# Revit family: xBall_Valves-Full_Port-WATTS-LFFBV3C_LFFBVS3C_Series
name_source: partatom
category: Pipe Accessories
revit_build: Autodesk Revit 2014 (Build: 20130308_1515(x64)
units: mm (PartAtom-declared; Revit-internal decimal feet)

## types (19) — shared parameters
Connector Description 1 = NPT Connection Inlet
Connector Description 2 = NPT Connection Outlet
Country = United States
Description = 2 Piece, Full Port, Lead Free Brass Ball Valve
Manufacturer = WATTS
Manufacturer Product Line = Water Safety & Flow Control
Material = Lead Free-WATTS-Copper Silicon Alloy
Product Documentation Link = http://media.wattswater.com
Product Page URL = http://www.watts.com
Region = North America
URL = http://www.watts.com

## per-type parameters (varying)
| type | Annotation Circle Radius | Body Midpoint | Center To Body Angle | Center To Handle Angle | Center To Handle Back | Center To Handle Tang | Center To Inlet | Center To Outlet | Connection Radius | Connection Type | Handle Height | Handle Length | Handle Thickness | Handle Width | Inlet Body Radius | Length | Max. Working Pressure | Model | Outlet Body Radius | Stem Height | Stem Radius |
| LFFBV-3C - 0.25" | 0.28 " | 0.875 " | 0.478 " | 0.492 " | 0.275 " | 0.436 " | 0.84 " | 0.91 " | 0" | Female NPT | 0.5 " | 3.438 " | 0.098 " | 0.55 " | 0.35 " | 1.75 " | 600psi (41 bar) WOG, non-shock; 150psi (10.3 bar) WSP | LFFBV-3C | 0.56 " | 1.183 " | 0.31 " |
| LFFBV-3C - 0.375" | 0.28 " | 0.875 " | 0.478 " | 0.492 " | 0.275 " | 0.436 " | 0.84 " | 0.91 " | 0" | Female NPT | 0.5 " | 3.438 " | 0.098 " | 0.55 " | 0.415 " | 1.75 " | 600psi (41 bar) WOG, non-shock; 150psi (10.3 bar) WSP | LFFBV-3C | 0.56 " | 1.183 " | 0.31 " |
| LFFBV-3C - 0.5" | 0.28 " | 0.969 " | 0.46 " | 0.492 " | 0.275 " | 0.436 " | 0.98 " | 0.958 " | 0" | Female NPT | 0.5 " | 3.438 " | 0.098 " | 0.55 " | 0.48 " | 1.938 " | 600psi (41 bar) WOG, non-shock; 150psi (10.3 bar) WSP | LFFBV-3C | 0.56 " | 1.123 " | 0.31 " |
| LFFBV-3C - 0.75" | 0.39 " | 1.157 " | 0.445 " | 0.483 " | 0.345 " | 0.53 " | 1.17 " | 1.143 " | 0" | Female NPT | 0.689 " | 4 " | 0.11 " | 0.689 " | 0.62 " | 2.313 " | 600psi (41 bar) WOG, non-shock; 150psi (10.3 bar) WSP | LFFBV-3C | 0.78 " | 1.359 " | 0.375 " |
| LFFBV-3C - 1" | 0.455 " | 1.407 " | 0.58 " | 0.577 " | 0.404 " | 0.64 " | 1.416 " | 1.397 " | 1" | Female NPT | 0.75 " | 4.25 " | 0.126 " | 0.807 " | 0.75 " | 2.813 " | 600psi (41 bar) WOG, non-shock; 150psi (10.3 bar) WSP | LFFBV-3C | 0.91 " | 1.633 " | 0.465 " |
| LFFBV-3C - 1.25" | 0.575 " | 1.594 " | 0.685 " | 0.577 " | 0.404 " | 0.64 " | 1.587 " | 1.601 " | 1" | Female NPT | 0.75 " | 4.25 " | 0.126 " | 0.807 " | 0.93 " | 3.188 " | 600psi (41 bar) WOG, non-shock; 150psi (10.3 bar) WSP | LFFBV-3C | 1.15 " | 1.823 " | 0.455 " |
| LFFBV-3C - 1.5" | 0.665 " | 1.75 " | 0.815 " | 0.847 " | 0.473 " | 0.687 " | 1.74 " | 1.76 " | 1" | Female NPT | 0.75 " | 5.25 " | 0.157 " | 0.945 " | 1.075 " | 3.5 " | 600psi (41 bar) WOG, non-shock; 150psi (10.3 bar) WSP | LFFBV-3C | 1.33 " | 2.118 " | 0.48 " |
| LFFBV-3C - 2" | 0.845 " | 2.063 " | 0.935 " | 0.847 " | 0.473 " | 0.687 " | 2.029 " | 2.096 " | 1" | Female NPT | 0.75 " | 6 " | 0.157 " | 0.945 " | 1.325 " | 4.125 " | 600psi (41 bar) WOG, non-shock; 150psi (10.3 bar) WSP | LFFBV-3C | 1.69 " | 2.581 " | 0.48 " |
| LFFBV-3C - 2.5" | 1.06 " | 2.657 " | 1.335 " | 0.8 " | 0.473 " | 0.853 " | 2.645 " | 2.668 " | 1" | Female NPT | 0.75 " | 7.375 " | 0.197 " | 0.945 " | 1.597 " | 5.313 " | 400psi (27.5 bar) WOG, non-shock
125psi (8.6 bar) WSP | LFFBV-3C | 2.12 " | 3.055 " | 0.615 " |
| LFFBV-3C - 3" | 1.258 " | 3.032 " | 1.59 " | 0.81 " | 0.551 " | 0.882 " | 3.028 " | 3.035 " | 2" | Female NPT | 0.75 " | 7.75 " | 0.197 " | 1.102 " | 1.98 " | 6.063 " | 400psi (27.5 bar) WOG, non-shock
125psi (8.6 bar) WSP | LFFBV-3C | 2.515 " | 3.477 " | 0.655 " |
| LFFBV-3C - 4" | 1.258 " | 3.719 " | 1.59 " | 0.81 " | 0.551 " | 0.882 " | 3.028 " | 4.41 " | 2" | Female NPT | 0.75 " | 9.625 " | 0.197 " | 1.102 " | 1.98 " | 7.438 " | 400psi (27.5 bar) WOG, non-shock
125psi (8.6 bar) WSP | LFFBV-3C | 2.515 " | 3.477 " | 0.655 " |
| LFFBVS-3C - 0.5" | 0.28 " | 1.032 " | 0.46 " | 0.492 " | 0.275 " | 0.436 " | 0.98 " | 1.083 " | 0" | Soldered Connection | 0.5 " | 3.438 " | 0.098 " | 0.55 " | 0.48 " | 2.063 " | 600psi (41 bar) WOG, non-shock; 150psi (10.3 bar) WSP | LFFBVS-3C | 0.56 " | 1.123 " | 0.31 " |
| LFFBVS-3C - 0.75" | 0.39 " | 1.344 " | 0.445 " | 0.483 " | 0.345 " | 0.53 " | 1.17 " | 1.518 " | 0" | Soldered Connection | 0.689 " | 4 " | 0.11 " | 0.689 " | 0.62 " | 2.688 " | 600psi (41 bar) WOG, non-shock; 150psi (10.3 bar) WSP | LFFBVS-3C | 0.78 " | 1.359 " | 0.375 " |
| LFFBVS-3C - 1" | 0.455 " | 1.625 " | 0.58 " | 0.577 " | 0.404 " | 0.64 " | 1.416 " | 1.834 " | 1" | Soldered Connection | 0.75 " | 4.25 " | 0.126 " | 0.807 " | 0.75 " | 3.25 " | 600psi (41 bar) WOG, non-shock; 150psi (10.3 bar) WSP | LFFBVS-3C | 0.91 " | 1.633 " | 0.465 " |
| LFFBVS-3C - 1.25" | 0.575 " | 1.844 " | 0.685 " | 0.577 " | 0.404 " | 0.64 " | 1.587 " | 2.101 " | 1" | Soldered Connection | 0.75 " | 4.25 " | 0.126 " | 0.807 " | 0.93 " | 3.688 " | 600psi (41 bar) WOG, non-shock; 150psi (10.3 bar) WSP | LFFBVS-3C | 1.15 " | 1.823 " | 0.455 " |
| LFFBVS-3C - 1.5" | 0.665 " | 2.125 " | 0.815 " | 0.847 " | 0.473 " | 0.687 " | 1.74 " | 2.51 " | 1" | Soldered Connection | 0.75 " | 5.25 " | 0.157 " | 0.945 " | 1.075 " | 4.25 " | 600psi (41 bar) WOG, non-shock; 150psi (10.3 bar) WSP | LFFBVS-3C | 1.33 " | 2.118 " | 0.48 " |
| LFFBVS-3C - 2" | 0.845 " | 2.657 " | 0.935 " | 0.847 " | 0.473 " | 0.687 " | 2.029 " | 3.284 " | 1" | Soldered Connection | 0.75 " | 6 " | 0.157 " | 0.945 " | 1.325 " | 5.313 " | 600psi (41 bar) WOG, non-shock; 150psi (10.3 bar) WSP | LFFBVS-3C | 1.69 " | 2.581 " | 0.48 " |
| LFFBVS-3C - 2.5" | 1.06 " | 3.125 " | 1.335 " | 0.8 " | 0.473 " | 0.853 " | 2.645 " | 3.605 " | 1" | Soldered Connection | 0.75 " | 7.375 " | 0.197 " | 0.945 " | 1.597 " | 6.25 " | 400psi (27.5 bar) WOG, non-shock
125psi (8.6 bar) WSP | LFFBVS-3C | 2.12 " | 3.055 " | 0.615 " |
| LFFBVS-3C - 3" | 1.258 " | 3.688 " | 1.59 " | 0.81 " | 0.551 " | 0.882 " | 3.028 " | 4.347 " | 2" | Soldered Connection | 0.75 " | 7.75 " | 0.197 " | 1.102 " | 1.98 " | 7.375 " | 400psi (27.5 bar) WOG, non-shock
125psi (8.6 bar) WSP | LFFBVS-3C | 2.515 " | 3.477 " | 0.655 " |

## geometry (parser evidence)
native form markers: Blend x2, Sweep x3
no freeform markers — native parametric forms only
